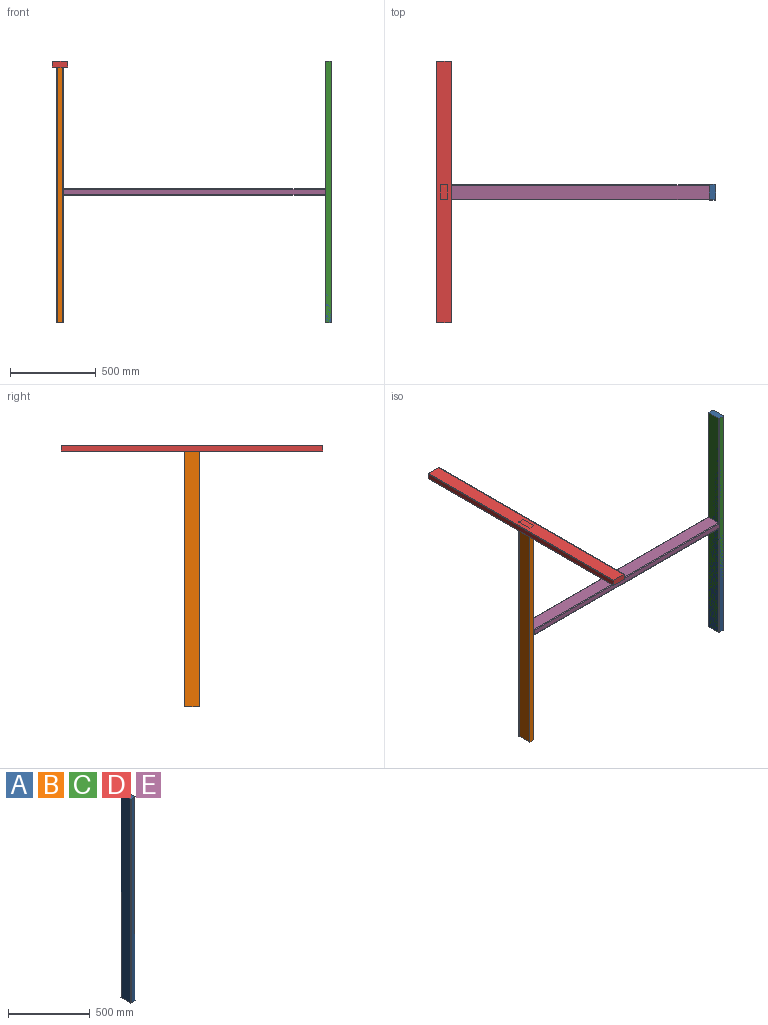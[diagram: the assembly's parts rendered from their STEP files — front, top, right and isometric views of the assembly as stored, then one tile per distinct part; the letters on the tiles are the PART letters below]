
ASSEMBLY  parts=5 mates=3
PART A: 10 faces, bbox 38.1x88.9x1524 mm
  f0: plane 1524x82.55mm, normal (1,0,0), area 125806.2mm2, adj f1,f7,f8,f9
  f1: cylinder r=3.17mm len=1524mm, axis (0,0,-1), area 7600.6mm2, adj f0,f2,f8,f9
  f2: plane 1524x31.75mm, normal (0,1,0), area 48387mm2, adj f1,f3,f8,f9
  f3: cylinder r=3.17mm len=1524mm, axis (0,0,-1), area 7600.6mm2, adj f2,f4,f8,f9
  f4: plane 1524x82.55mm, normal (-1,0,0), area 125806.2mm2, adj f3,f5,f8,f9
  f5: cylinder r=3.17mm len=1524mm, axis (0,0,-1), area 7600.6mm2, adj f4,f6,f8,f9
  f6: plane 1524x31.75mm, normal (0,-1,0), area 48387mm2, adj f5,f7,f8,f9
  f7: cylinder r=3.17mm len=1524mm, axis (0,0,-1), area 7600.6mm2, adj f0,f6,f8,f9
  f8: plane 88.9x38.1mm, normal (0,0,1), area 3378.4mm2, adj f0,f1,f2,f3,f4,f5,f6,f7
  f9: plane 88.9x38.1mm, normal (0,0,-1), area 3378.4mm2, adj f0,f1,f2,f3,f4,f5,f6,f7
PART B: same geometry as A
PART C: same geometry as A
PART D: same geometry as A
PART E: same geometry as A
PLACE A t=(826.25,-553.9,-65.81)mm
PLACE B t=(-735.85,-553.9,-65.81)mm
PLACE C t=(826.25,-553.9,-65.81)mm
PLACE D rot(axis=(-0.58,-0.58,-0.58),120deg) t=(-735.85,-1315.9,1439.14)mm
PLACE E rot(axis=(0,-1,0),90deg) t=(807.2,-553.9,696.19)mm
MATE fastened B.f8 <-> D.f0  axis (0,0,1) through (-735.85,-553.9,1458.19)mm
MATE fastened E.f9 <-> A.f4  axis (1,0,0) through (807.2,-553.9,696.19)mm
MATE fastened E.f8 <-> B.f0  axis (-1,0,0) through (-716.8,-553.9,696.19)mm
